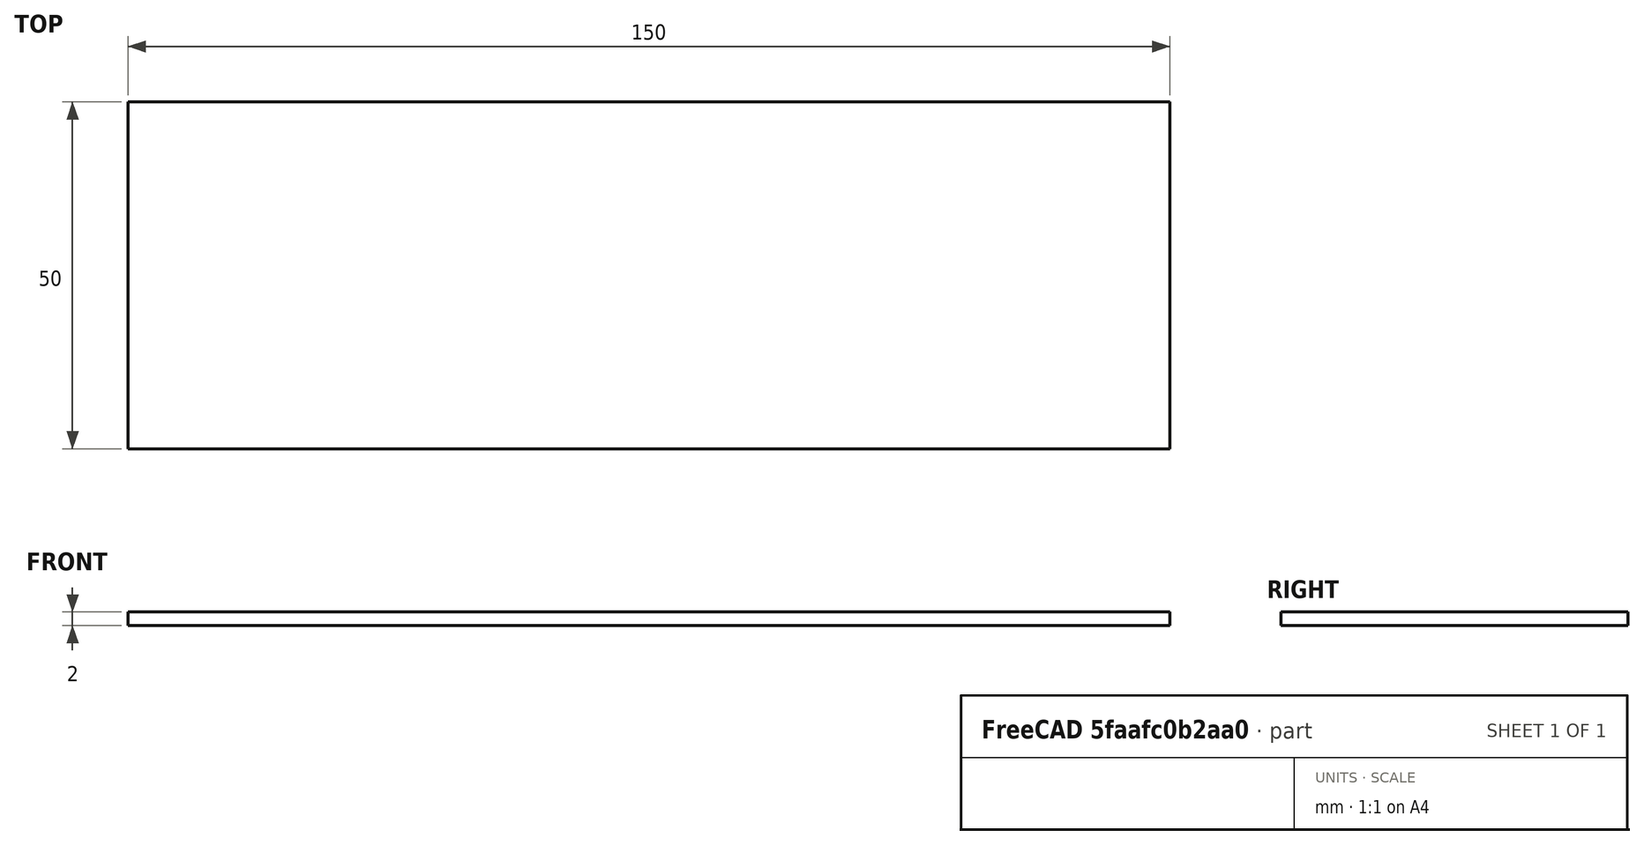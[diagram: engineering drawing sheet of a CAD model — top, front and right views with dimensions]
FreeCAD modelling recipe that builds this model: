
FCSTD DOCUMENT  (FreeCAD 0.19R24276 (Git))
Label: plastina_50x150_v1
License: All rights reserved
LicenseURL: http://en.wikipedia.org/wiki/All_rights_reserved
objects: Sketcher::SketchObject×2, PartDesign::Pad×1, PartDesign::Body×1
note: 5 computed .brp shape members not serialized (recipe doc carries the construction recipe); baked Part::Feature solids carry a one-line shape summary decoded from their .brp

FEATURE [Sketcher::SketchObject] Sketch
  FullyConstrained = true
  MapMode = 5
  Support = -> [XY_Plane]
FEATURE [Sketcher::SketchObject] Sketch001
  FullyConstrained = true
  MapMode = 5
  Support = -> [XY_Plane]
  sketch-geometry (4):
    g0: LineSegment StartX=0 StartY=0 StartZ=0 EndX=150 EndY=0 EndZ=0
    g1: LineSegment StartX=150 StartY=0 StartZ=0 EndX=150 EndY=50 EndZ=0
    g2: LineSegment StartX=150 StartY=50 StartZ=0 EndX=0 EndY=50 EndZ=0
    g3: LineSegment StartX=0 StartY=50 StartZ=0 EndX=0 EndY=0 EndZ=0
  constraints (11):
    c: Coincident(g0,g1)
    c: Coincident(g1,g2)
    c: Coincident(g2,g3)
    c: Coincident(g3,g0)
    c: Horizontal(g0)
    c: Horizontal(g2)
    c: Vertical(g1)
    c: Vertical(g3)
    c: Coincident(g0,g-1)
    c: DistanceY(g1,g1) = 50
    c: DistanceX(g2,g2) = 150
FEATURE [PartDesign::Pad] Pad
  Direction = (1,1,1)
  Length = 2
  Length2 = 100
  Profile = -> Sketch001
  Type = 0
FEATURE [PartDesign::Body] Body
  Group = -> [Sketch,Sketch001,Pad]
  Origin = -> Origin
  Tip = -> Pad
